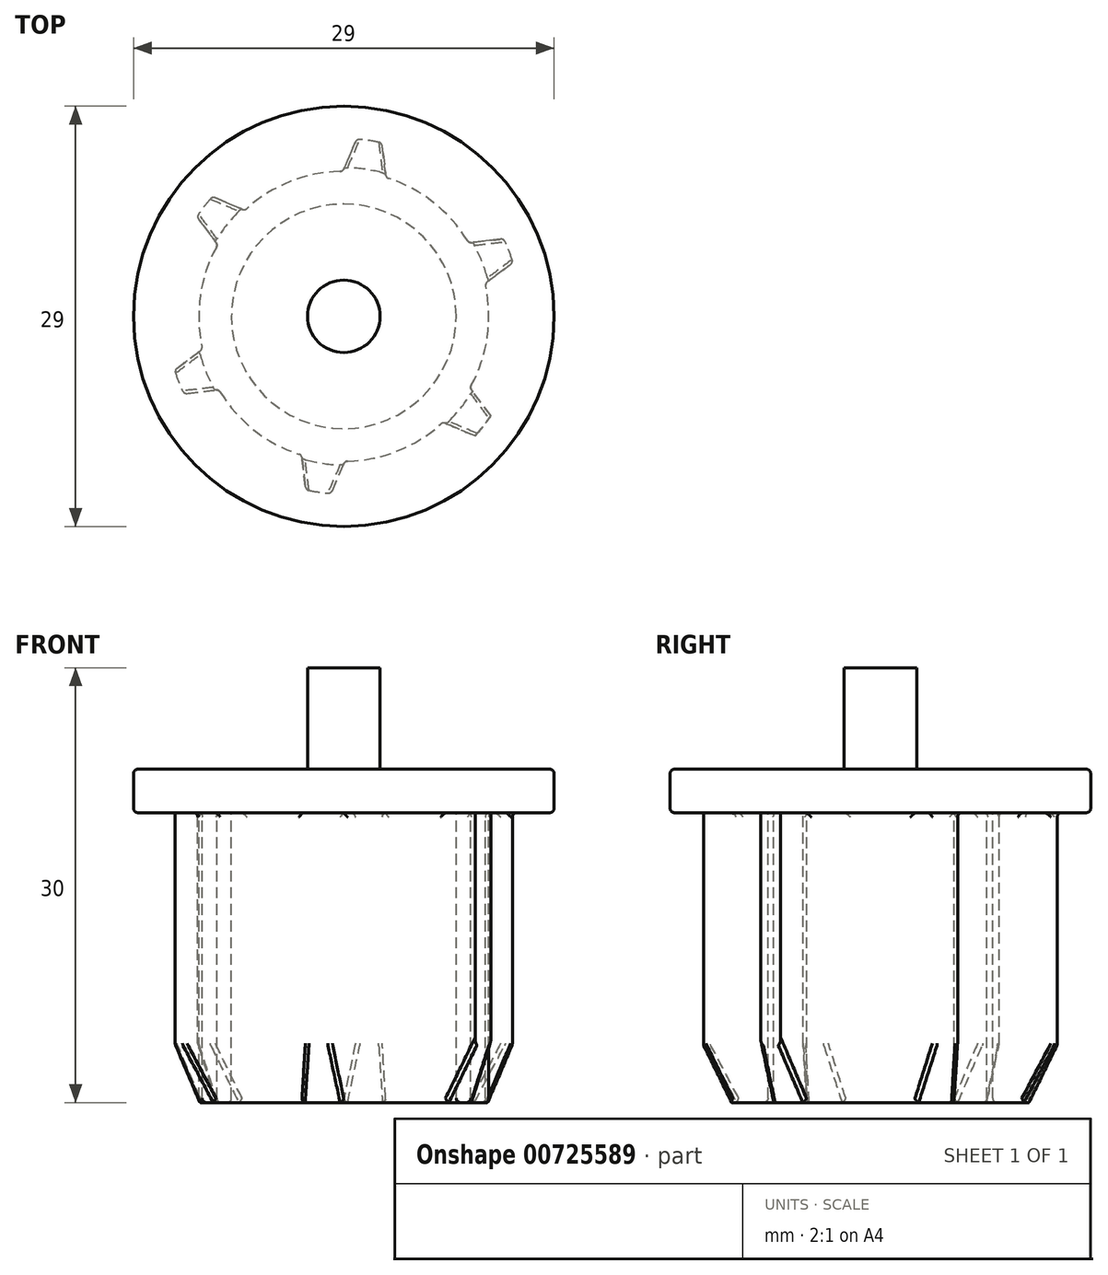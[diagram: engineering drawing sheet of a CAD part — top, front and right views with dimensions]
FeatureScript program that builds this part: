
annotation { "Feature Type Name" : "Feature", "Feature Type Description" : "" }
export const myFeature = defineFeature(function(context is Context, id is Id, definition is map)
    precondition{}
    {
        {
            var Q0;
            Q0=qCreatedBy(makeId("Top.planeOp"),FACE);
            var sketch = newSketch(context, id + "F0", { "sketchPlane" : qUnion([Q0])});
            skCircle(sketch, "E0", {"center": v(-16.6, 0) * mm, "radius": 14.5 * mm});
            skCircle(sketch, "E1", {"center": v(-16.6, 0) * mm, "radius": 12.25 * mm});
            skCircle(sketch, "E2", {"center": v(-16.6, 0) * mm, "radius": 4 * mm, "construction": true});
            skCircle(sketch, "E3.cCircle", {"center": v(-16.6, 0) * mm, "radius": 15 * mm, "construction": true});
            skLineSegment(sketch, "E3.0", {"start": v(-6.99, 12.2) * mm, "end": v(-2.18, 5.76) * mm});
            skLineSegment(sketch, "E3.1", {"start": v(-2.18, 5.76) * mm, "end": v(-1.23, -2.23) * mm});
            skLineSegment(sketch, "E3.2", {"start": v(-1.23, -2.23) * mm, "end": v(-4.4, -9.61) * mm});
            skLineSegment(sketch, "E3.3", {"start": v(-4.4, -9.61) * mm, "end": v(-10.84, -14.42) * mm});
            skLineSegment(sketch, "E3.4", {"start": v(-10.84, -14.42) * mm, "end": v(-18.83, -15.37) * mm});
            skLineSegment(sketch, "E3.5", {"start": v(-18.83, -15.37) * mm, "end": v(-26.21, -12.2) * mm});
            skLineSegment(sketch, "E3.6", {"start": v(-26.21, -12.2) * mm, "end": v(-31.02, -5.76) * mm});
            skLineSegment(sketch, "E3.7", {"start": v(-31.02, -5.76) * mm, "end": v(-31.97, 2.23) * mm});
            skLineSegment(sketch, "E3.8", {"start": v(-31.97, 2.23) * mm, "end": v(-28.8, 9.61) * mm});
            skLineSegment(sketch, "E3.9", {"start": v(-28.8, 9.61) * mm, "end": v(-22.36, 14.42) * mm});
            skLineSegment(sketch, "E3.10", {"start": v(-22.36, 14.42) * mm, "end": v(-14.37, 15.37) * mm});
            skLineSegment(sketch, "E3.11", {"start": v(-14.37, 15.37) * mm, "end": v(-6.99, 12.2) * mm});
            skPoint(sketch, "E3.0.midPoint", {"position": v(-4.58, 8.98) * mm});
            skLineSegment(sketch, "E4", {"start": v(-18.83, -15.37) * mm, "end": v(-20.57, -0.47) * mm});
            skLineSegment(sketch, "E5", {"start": v(-18.83, -15.37) * mm, "end": v(-12.92, -1.57) * mm});
            skLineSegment(sketch, "E6", {"start": v(-4.4, -9.61) * mm, "end": v(-18.18, -3.67) * mm});
            skLineSegment(sketch, "E7", {"start": v(-4.4, -9.61) * mm, "end": v(-13.4, 2.4) * mm});
            skLineSegment(sketch, "E8", {"start": v(-2.18, 5.76) * mm, "end": v(-14.21, -3.2) * mm});
            skLineSegment(sketch, "E9", {"start": v(-2.18, 5.76) * mm, "end": v(-17.08, 3.97) * mm});
            skLineSegment(sketch, "E10", {"start": v(-14.37, 15.37) * mm, "end": v(-12.63, 0.47) * mm});
            skLineSegment(sketch, "E11", {"start": v(-14.37, 15.37) * mm, "end": v(-20.28, 1.57) * mm});
            skLineSegment(sketch, "E12", {"start": v(-28.8, 9.61) * mm, "end": v(-15.02, 3.67) * mm});
            skLineSegment(sketch, "E13", {"start": v(-28.8, 9.61) * mm, "end": v(-19.8, -2.4) * mm});
            skLineSegment(sketch, "E14", {"start": v(-31.02, -5.76) * mm, "end": v(-18.99, 3.2) * mm});
            skLineSegment(sketch, "E15", {"start": v(-31.02, -5.76) * mm, "end": v(-16.12, -3.97) * mm});
            skCircle(sketch, "E16", {"center": v(-16.6, 0) * mm, "radius": 10 * mm});
            skCircle(sketch, "E17", {"center": v(-16.6, 0) * mm, "radius": 7.75 * mm});
            skCircle(sketch, "E18", {"center": v(-16.6, 0) * mm, "radius": 2.5 * mm});
            skSolve(sketch);
        }
        {
            var Q0;
            Q0=qCreatedBy(makeId("Front.planeOp"),FACE);
            var sketch = newSketch(context, id + "F1", { "sketchPlane" : qUnion([Q0])});
            skLineSegment(sketch, "E19", {"start": v(-32.68, -23) * mm, "end": v(-0.52, -23) * mm});
            skLineSegment(sketch, "E20", {"start": v(-32.68, -20) * mm, "end": v(-0.52, -20) * mm});
            skLineSegment(sketch, "E21", {"start": v(-32.68, -3) * mm, "end": v(-0.52, -3) * mm});
            skLineSegment(sketch, "E22", {"start": v(-32.68, 0) * mm, "end": v(-0.52, 0) * mm});
            skSolve(sketch);
        }
        {
            var Q0;
            {var subQ0=sQuery(id+"F0.wireOp",EDGE,"E16");var subQ1=sQuery(id+"F0.wireOp",EDGE,"E9");var subQ2=makeQuery(id+"F0.imprint","INTERSECT",VERTEX,{"derivedFrom":[subQ1,subQ0]});Q0=makeQuery(id+"F0.imprint","IMPRINT",FACE,{"disambiguationData":[TD([[makeQuery(id+"F0.imprint","IMPRINT",EDGE,{"disambiguationData":[TD([[subQ2,-1.0]])],"derivedFrom":subQ1}),-1.0]])]});}
            var Q1;
            {var subQ0=sQuery(id+"F0.wireOp",EDGE,"E9");var subQ1=sQuery(id+"F0.wireOp",EDGE,"E1");var subQ2=makeQuery(id+"F0.imprint","INTERSECT",VERTEX,{"derivedFrom":[subQ1,subQ0]});Q1=makeQuery(id+"F0.imprint","IMPRINT",FACE,{"disambiguationData":[TD([[makeQuery(id+"F0.imprint","IMPRINT",EDGE,{"disambiguationData":[TD([[subQ2,1.0]])],"derivedFrom":subQ1}),1.0]])]});}
            var Q2;
            {var subQ0=sQuery(id+"F0.wireOp",EDGE,"E16");var subQ1=sQuery(id+"F0.wireOp",EDGE,"E8");var subQ2=makeQuery(id+"F0.imprint","INTERSECT",VERTEX,{"derivedFrom":[subQ1,subQ0]});Q2=makeQuery(id+"F0.imprint","IMPRINT",FACE,{"disambiguationData":[TD([[makeQuery(id+"F0.imprint","IMPRINT",EDGE,{"disambiguationData":[TD([[subQ2,-1.0]])],"derivedFrom":subQ1}),-1.0]])]});}
            var Q3;
            {var subQ0=sQuery(id+"F0.wireOp",EDGE,"E16");var subQ1=sQuery(id+"F0.wireOp",EDGE,"E7");var subQ2=makeQuery(id+"F0.imprint","INTERSECT",VERTEX,{"derivedFrom":[subQ1,subQ0]});Q3=makeQuery(id+"F0.imprint","IMPRINT",FACE,{"disambiguationData":[TD([[makeQuery(id+"F0.imprint","IMPRINT",EDGE,{"disambiguationData":[TD([[subQ2,-1.0]])],"derivedFrom":subQ1}),-1.0]])]});}
            var Q4;
            {var subQ0=sQuery(id+"F0.wireOp",EDGE,"E6");var subQ1=sQuery(id+"F0.wireOp",EDGE,"E1");var subQ2=makeQuery(id+"F0.imprint","INTERSECT",VERTEX,{"derivedFrom":[subQ1,subQ0]});Q4=makeQuery(id+"F0.imprint","IMPRINT",FACE,{"disambiguationData":[TD([[makeQuery(id+"F0.imprint","IMPRINT",EDGE,{"disambiguationData":[TD([[subQ2,-1.0]])],"derivedFrom":subQ1}),1.0]])]});}
            var Q5;
            {var subQ0=sQuery(id+"F0.wireOp",EDGE,"E16");var subQ1=sQuery(id+"F0.wireOp",EDGE,"E6");var subQ2=makeQuery(id+"F0.imprint","INTERSECT",VERTEX,{"derivedFrom":[subQ1,subQ0]});Q5=makeQuery(id+"F0.imprint","IMPRINT",FACE,{"disambiguationData":[TD([[makeQuery(id+"F0.imprint","IMPRINT",EDGE,{"disambiguationData":[TD([[subQ2,-1.0]])],"derivedFrom":subQ1}),-1.0]])]});}
            var Q6;
            {var subQ0=sQuery(id+"F0.wireOp",EDGE,"E16");var subQ1=sQuery(id+"F0.wireOp",EDGE,"E5");var subQ2=makeQuery(id+"F0.imprint","INTERSECT",VERTEX,{"derivedFrom":[subQ1,subQ0]});Q6=makeQuery(id+"F0.imprint","IMPRINT",FACE,{"disambiguationData":[TD([[makeQuery(id+"F0.imprint","IMPRINT",EDGE,{"disambiguationData":[TD([[subQ2,-1.0]])],"derivedFrom":subQ1}),-1.0]])]});}
            var Q7;
            {var subQ0=sQuery(id+"F0.wireOp",EDGE,"E16");var subQ1=sQuery(id+"F0.wireOp",EDGE,"E4");var subQ2=makeQuery(id+"F0.imprint","INTERSECT",VERTEX,{"derivedFrom":[subQ1,subQ0]});Q7=makeQuery(id+"F0.imprint","IMPRINT",FACE,{"disambiguationData":[TD([[makeQuery(id+"F0.imprint","IMPRINT",EDGE,{"disambiguationData":[TD([[subQ2,-1.0]])],"derivedFrom":subQ1}),-1.0]])]});}
            var Q8;
            {var subQ0=sQuery(id+"F0.wireOp",EDGE,"E4");var subQ1=sQuery(id+"F0.wireOp",EDGE,"E1");var subQ2=makeQuery(id+"F0.imprint","INTERSECT",VERTEX,{"derivedFrom":[subQ1,subQ0]});Q8=makeQuery(id+"F0.imprint","IMPRINT",FACE,{"disambiguationData":[TD([[makeQuery(id+"F0.imprint","IMPRINT",EDGE,{"disambiguationData":[TD([[subQ2,-1.0]])],"derivedFrom":subQ1}),1.0]])]});}
            var Q9;
            {var subQ0=sQuery(id+"F0.wireOp",EDGE,"E16");var subQ1=sQuery(id+"F0.wireOp",EDGE,"E4");var subQ2=makeQuery(id+"F0.imprint","INTERSECT",VERTEX,{"derivedFrom":[subQ1,subQ0]});Q9=makeQuery(id+"F0.imprint","IMPRINT",FACE,{"disambiguationData":[TD([[makeQuery(id+"F0.imprint","IMPRINT",EDGE,{"disambiguationData":[TD([[subQ2,-1.0]])],"derivedFrom":subQ1}),1.0]])]});}
            var Q10;
            {var subQ0=sQuery(id+"F0.wireOp",EDGE,"E16");var subQ1=sQuery(id+"F0.wireOp",EDGE,"E14");var subQ2=makeQuery(id+"F0.imprint","INTERSECT",VERTEX,{"derivedFrom":[subQ1,subQ0]});Q10=makeQuery(id+"F0.imprint","IMPRINT",FACE,{"disambiguationData":[TD([[makeQuery(id+"F0.imprint","IMPRINT",EDGE,{"disambiguationData":[TD([[subQ2,-1.0]])],"derivedFrom":subQ1}),-1.0]])]});}
            var Q11;
            {var subQ0=sQuery(id+"F0.wireOp",EDGE,"E14");var subQ1=sQuery(id+"F0.wireOp",EDGE,"E1");var subQ2=makeQuery(id+"F0.imprint","INTERSECT",VERTEX,{"derivedFrom":[subQ1,subQ0]});Q11=makeQuery(id+"F0.imprint","IMPRINT",FACE,{"disambiguationData":[TD([[makeQuery(id+"F0.imprint","IMPRINT",EDGE,{"disambiguationData":[TD([[subQ2,-1.0]])],"derivedFrom":subQ1}),1.0]])]});}
            var Q12;
            {var subQ0=sQuery(id+"F0.wireOp",EDGE,"E16");var subQ1=sQuery(id+"F0.wireOp",EDGE,"E13");var subQ2=makeQuery(id+"F0.imprint","INTERSECT",VERTEX,{"derivedFrom":[subQ1,subQ0]});Q12=makeQuery(id+"F0.imprint","IMPRINT",FACE,{"disambiguationData":[TD([[makeQuery(id+"F0.imprint","IMPRINT",EDGE,{"disambiguationData":[TD([[subQ2,-1.0]])],"derivedFrom":subQ1}),-1.0]])]});}
            var Q13;
            {var subQ0=sQuery(id+"F0.wireOp",EDGE,"E16");var subQ1=sQuery(id+"F0.wireOp",EDGE,"E12");var subQ2=makeQuery(id+"F0.imprint","INTERSECT",VERTEX,{"derivedFrom":[subQ1,subQ0]});Q13=makeQuery(id+"F0.imprint","IMPRINT",FACE,{"disambiguationData":[TD([[makeQuery(id+"F0.imprint","IMPRINT",EDGE,{"disambiguationData":[TD([[subQ2,-1.0]])],"derivedFrom":subQ1}),-1.0]])]});}
            var Q14;
            {var subQ0=sQuery(id+"F0.wireOp",EDGE,"E12");var subQ1=sQuery(id+"F0.wireOp",EDGE,"E1");var subQ2=makeQuery(id+"F0.imprint","INTERSECT",VERTEX,{"derivedFrom":[subQ1,subQ0]});Q14=makeQuery(id+"F0.imprint","IMPRINT",FACE,{"disambiguationData":[TD([[makeQuery(id+"F0.imprint","IMPRINT",EDGE,{"disambiguationData":[TD([[subQ2,-1.0]])],"derivedFrom":subQ1}),1.0]])]});}
            var Q15;
            {var subQ0=sQuery(id+"F0.wireOp",EDGE,"E16");var subQ1=sQuery(id+"F0.wireOp",EDGE,"E11");var subQ2=makeQuery(id+"F0.imprint","INTERSECT",VERTEX,{"derivedFrom":[subQ1,subQ0]});Q15=makeQuery(id+"F0.imprint","IMPRINT",FACE,{"disambiguationData":[TD([[makeQuery(id+"F0.imprint","IMPRINT",EDGE,{"disambiguationData":[TD([[subQ2,-1.0]])],"derivedFrom":subQ1}),-1.0]])]});}
            var Q16;
            {var subQ0=sQuery(id+"F0.wireOp",EDGE,"E16");var subQ1=sQuery(id+"F0.wireOp",EDGE,"E10");var subQ2=makeQuery(id+"F0.imprint","INTERSECT",VERTEX,{"derivedFrom":[subQ1,subQ0]});Q16=makeQuery(id+"F0.imprint","IMPRINT",FACE,{"disambiguationData":[TD([[makeQuery(id+"F0.imprint","IMPRINT",EDGE,{"disambiguationData":[TD([[subQ2,-1.0]])],"derivedFrom":subQ1}),-1.0]])]});}
            var Q17;
            {var subQ0=sQuery(id+"F0.wireOp",EDGE,"E10");var subQ1=sQuery(id+"F0.wireOp",EDGE,"E1");var subQ2=makeQuery(id+"F0.imprint","INTERSECT",VERTEX,{"derivedFrom":[subQ1,subQ0]});Q17=makeQuery(id+"F0.imprint","IMPRINT",FACE,{"disambiguationData":[TD([[makeQuery(id+"F0.imprint","IMPRINT",EDGE,{"disambiguationData":[TD([[subQ2,-1.0]])],"derivedFrom":subQ1}),1.0]])]});}
            var Q18;
            Q18=sQuery(id+"F1.wireOp",VERTEX,"E19.start");
            extrude(context, id + "F2", {"entities" : qUnion([Q0, Q1, Q2, Q3, Q4, Q5, Q6, Q7, Q8, Q9, Q10, Q11, Q12, Q13, Q14, Q15, Q16, Q17]), "endBound" : BoundingType.UP_TO_VERTEX, "oppositeDirection" : true, "depth" : 25 * mm, "endBoundEntityVertex" : qUnion([Q18]), "offsetDistance" : 25 * mm});
        }
        {
            var Q0;
            {var subQ0=sQuery(id+"F0.wireOp",EDGE,"E11");var subQ1=sQuery(id+"F0.wireOp",EDGE,"E1");var subQ2=makeQuery(id+"F0.imprint","INTERSECT",VERTEX,{"derivedFrom":[subQ1,subQ0]});Q0=makeQuery(id+"F0.imprint","IMPRINT",FACE,{"disambiguationData":[TD([[makeQuery(id+"F0.imprint","IMPRINT",EDGE,{"disambiguationData":[TD([[subQ2,-1.0]])],"derivedFrom":subQ1}),1.0]])]});}
            var Q1;
            {var subQ0=sQuery(id+"F0.wireOp",EDGE,"E11");var subQ1=sQuery(id+"F0.wireOp",EDGE,"E0");var subQ2=makeQuery(id+"F0.imprint","INTERSECT",VERTEX,{"derivedFrom":[subQ1,subQ0]});Q1=makeQuery(id+"F0.imprint","IMPRINT",FACE,{"disambiguationData":[TD([[makeQuery(id+"F0.imprint","IMPRINT",EDGE,{"disambiguationData":[TD([[subQ2,-1.0]])],"derivedFrom":subQ1}),1.0]])]});}
            var Q2;
            {var subQ0=sQuery(id+"F0.wireOp",EDGE,"E10");var subQ1=sQuery(id+"F0.wireOp",EDGE,"E0");var subQ2=makeQuery(id+"F0.imprint","INTERSECT",VERTEX,{"derivedFrom":[subQ1,subQ0]});Q2=makeQuery(id+"F0.imprint","IMPRINT",FACE,{"disambiguationData":[TD([[makeQuery(id+"F0.imprint","IMPRINT",EDGE,{"disambiguationData":[TD([[subQ2,-1.0]])],"derivedFrom":subQ1}),1.0]])]});}
            var Q3;
            {var subQ0=sQuery(id+"F0.wireOp",EDGE,"E9");var subQ1=sQuery(id+"F0.wireOp",EDGE,"E0");var subQ2=makeQuery(id+"F0.imprint","INTERSECT",VERTEX,{"derivedFrom":[subQ1,subQ0]});Q3=makeQuery(id+"F0.imprint","IMPRINT",FACE,{"disambiguationData":[TD([[makeQuery(id+"F0.imprint","IMPRINT",EDGE,{"disambiguationData":[TD([[subQ2,-1.0]])],"derivedFrom":subQ1}),1.0]])]});}
            var Q4;
            {var subQ0=sQuery(id+"F0.wireOp",EDGE,"E9");var subQ1=sQuery(id+"F0.wireOp",EDGE,"E1");var subQ2=makeQuery(id+"F0.imprint","INTERSECT",VERTEX,{"derivedFrom":[subQ1,subQ0]});Q4=makeQuery(id+"F0.imprint","IMPRINT",FACE,{"disambiguationData":[TD([[makeQuery(id+"F0.imprint","IMPRINT",EDGE,{"disambiguationData":[TD([[subQ2,-1.0]])],"derivedFrom":subQ1}),1.0]])]});}
            var Q5;
            {var subQ0=sQuery(id+"F0.wireOp",EDGE,"E10");var subQ1=sQuery(id+"F0.wireOp",EDGE,"E1");var subQ2=makeQuery(id+"F0.imprint","INTERSECT",VERTEX,{"derivedFrom":[subQ1,subQ0]});Q5=makeQuery(id+"F0.imprint","IMPRINT",FACE,{"disambiguationData":[TD([[makeQuery(id+"F0.imprint","IMPRINT",EDGE,{"disambiguationData":[TD([[subQ2,-1.0]])],"derivedFrom":subQ1}),1.0]])]});}
            var Q6;
            {var subQ0=sQuery(id+"F0.wireOp",EDGE,"E16");var subQ1=sQuery(id+"F0.wireOp",EDGE,"E9");var subQ2=makeQuery(id+"F0.imprint","INTERSECT",VERTEX,{"derivedFrom":[subQ1,subQ0]});Q6=makeQuery(id+"F0.imprint","IMPRINT",FACE,{"disambiguationData":[TD([[makeQuery(id+"F0.imprint","IMPRINT",EDGE,{"disambiguationData":[TD([[subQ2,-1.0]])],"derivedFrom":subQ1}),-1.0]])]});}
            var Q7;
            {var subQ0=sQuery(id+"F0.wireOp",EDGE,"E16");var subQ1=sQuery(id+"F0.wireOp",EDGE,"E8");var subQ2=makeQuery(id+"F0.imprint","INTERSECT",VERTEX,{"derivedFrom":[subQ1,subQ0]});Q7=makeQuery(id+"F0.imprint","IMPRINT",FACE,{"disambiguationData":[TD([[makeQuery(id+"F0.imprint","IMPRINT",EDGE,{"disambiguationData":[TD([[subQ2,-1.0]])],"derivedFrom":subQ1}),-1.0]])]});}
            var Q8;
            {var subQ0=sQuery(id+"F0.wireOp",EDGE,"E9");var subQ1=sQuery(id+"F0.wireOp",EDGE,"E1");var subQ2=makeQuery(id+"F0.imprint","INTERSECT",VERTEX,{"derivedFrom":[subQ1,subQ0]});Q8=makeQuery(id+"F0.imprint","IMPRINT",FACE,{"disambiguationData":[TD([[makeQuery(id+"F0.imprint","IMPRINT",EDGE,{"disambiguationData":[TD([[subQ2,1.0]])],"derivedFrom":subQ1}),1.0]])]});}
            var Q9;
            {var subQ0=sQuery(id+"F0.wireOp",EDGE,"E9");var subQ1=sQuery(id+"F0.wireOp",EDGE,"E0");var subQ2=makeQuery(id+"F0.imprint","INTERSECT",VERTEX,{"derivedFrom":[subQ1,subQ0]});Q9=makeQuery(id+"F0.imprint","IMPRINT",FACE,{"disambiguationData":[TD([[makeQuery(id+"F0.imprint","IMPRINT",EDGE,{"disambiguationData":[TD([[subQ2,1.0]])],"derivedFrom":subQ1}),1.0]])]});}
            var Q10;
            {var subQ0=sQuery(id+"F0.wireOp",EDGE,"E8");var subQ1=sQuery(id+"F0.wireOp",EDGE,"E1");var subQ2=makeQuery(id+"F0.imprint","INTERSECT",VERTEX,{"derivedFrom":[subQ1,subQ0]});Q10=makeQuery(id+"F0.imprint","IMPRINT",FACE,{"disambiguationData":[TD([[makeQuery(id+"F0.imprint","IMPRINT",EDGE,{"disambiguationData":[TD([[subQ2,1.0]])],"derivedFrom":subQ1}),1.0]])]});}
            var Q11;
            {var subQ0=sQuery(id+"F0.wireOp",EDGE,"E5");var subQ1=sQuery(id+"F0.wireOp",EDGE,"E0");var subQ2=makeQuery(id+"F0.imprint","INTERSECT",VERTEX,{"derivedFrom":[subQ1,subQ0]});Q11=makeQuery(id+"F0.imprint","IMPRINT",FACE,{"disambiguationData":[TD([[makeQuery(id+"F0.imprint","IMPRINT",EDGE,{"disambiguationData":[TD([[subQ2,-1.0]])],"derivedFrom":subQ1}),1.0]])]});}
            var Q12;
            {var subQ0=sQuery(id+"F0.wireOp",EDGE,"E4");var subQ1=sQuery(id+"F0.wireOp",EDGE,"E0");var subQ2=makeQuery(id+"F0.imprint","INTERSECT",VERTEX,{"derivedFrom":[subQ1,subQ0]});Q12=makeQuery(id+"F0.imprint","IMPRINT",FACE,{"disambiguationData":[TD([[makeQuery(id+"F0.imprint","IMPRINT",EDGE,{"disambiguationData":[TD([[subQ2,-1.0]])],"derivedFrom":subQ1}),1.0]])]});}
            var Q13;
            {var subQ0=sQuery(id+"F0.wireOp",EDGE,"E4");var subQ1=sQuery(id+"F0.wireOp",EDGE,"E1");var subQ2=makeQuery(id+"F0.imprint","INTERSECT",VERTEX,{"derivedFrom":[subQ1,subQ0]});Q13=makeQuery(id+"F0.imprint","IMPRINT",FACE,{"disambiguationData":[TD([[makeQuery(id+"F0.imprint","IMPRINT",EDGE,{"disambiguationData":[TD([[subQ2,-1.0]])],"derivedFrom":subQ1}),1.0]])]});}
            var Q14;
            {var subQ0=sQuery(id+"F0.wireOp",EDGE,"E14");var subQ1=sQuery(id+"F0.wireOp",EDGE,"E1");var subQ2=makeQuery(id+"F0.imprint","INTERSECT",VERTEX,{"derivedFrom":[subQ1,subQ0]});Q14=makeQuery(id+"F0.imprint","IMPRINT",FACE,{"disambiguationData":[TD([[makeQuery(id+"F0.imprint","IMPRINT",EDGE,{"disambiguationData":[TD([[subQ2,-1.0]])],"derivedFrom":subQ1}),1.0]])]});}
            var Q15;
            {var subQ0=sQuery(id+"F0.wireOp",EDGE,"E16");var subQ1=sQuery(id+"F0.wireOp",EDGE,"E14");var subQ2=makeQuery(id+"F0.imprint","INTERSECT",VERTEX,{"derivedFrom":[subQ1,subQ0]});Q15=makeQuery(id+"F0.imprint","IMPRINT",FACE,{"disambiguationData":[TD([[makeQuery(id+"F0.imprint","IMPRINT",EDGE,{"disambiguationData":[TD([[subQ2,-1.0]])],"derivedFrom":subQ1}),-1.0]])]});}
            var Q16;
            {var subQ0=sQuery(id+"F0.wireOp",EDGE,"E8");var subQ1=sQuery(id+"F0.wireOp",EDGE,"E0");var subQ2=makeQuery(id+"F0.imprint","INTERSECT",VERTEX,{"derivedFrom":[subQ1,subQ0]});Q16=makeQuery(id+"F0.imprint","IMPRINT",FACE,{"disambiguationData":[TD([[makeQuery(id+"F0.imprint","IMPRINT",EDGE,{"disambiguationData":[TD([[subQ2,1.0]])],"derivedFrom":subQ1}),1.0]])]});}
            var Q17;
            {var subQ0=sQuery(id+"F0.wireOp",EDGE,"E6");var subQ1=sQuery(id+"F0.wireOp",EDGE,"E0");var subQ2=makeQuery(id+"F0.imprint","INTERSECT",VERTEX,{"derivedFrom":[subQ1,subQ0]});Q17=makeQuery(id+"F0.imprint","IMPRINT",FACE,{"disambiguationData":[TD([[makeQuery(id+"F0.imprint","IMPRINT",EDGE,{"disambiguationData":[TD([[subQ2,-1.0]])],"derivedFrom":subQ1}),1.0]])]});}
            var Q18;
            {var subQ0=sQuery(id+"F0.wireOp",EDGE,"E6");var subQ1=sQuery(id+"F0.wireOp",EDGE,"E1");var subQ2=makeQuery(id+"F0.imprint","INTERSECT",VERTEX,{"derivedFrom":[subQ1,subQ0]});Q18=makeQuery(id+"F0.imprint","IMPRINT",FACE,{"disambiguationData":[TD([[makeQuery(id+"F0.imprint","IMPRINT",EDGE,{"disambiguationData":[TD([[subQ2,-1.0]])],"derivedFrom":subQ1}),1.0]])]});}
            var Q19;
            {var subQ0=sQuery(id+"F0.wireOp",EDGE,"E5");var subQ1=sQuery(id+"F0.wireOp",EDGE,"E1");var subQ2=makeQuery(id+"F0.imprint","INTERSECT",VERTEX,{"derivedFrom":[subQ1,subQ0]});Q19=makeQuery(id+"F0.imprint","IMPRINT",FACE,{"disambiguationData":[TD([[makeQuery(id+"F0.imprint","IMPRINT",EDGE,{"disambiguationData":[TD([[subQ2,-1.0]])],"derivedFrom":subQ1}),1.0]])]});}
            var Q20;
            {var subQ0=sQuery(id+"F0.wireOp",EDGE,"E15");var subQ1=sQuery(id+"F0.wireOp",EDGE,"E1");var subQ2=makeQuery(id+"F0.imprint","INTERSECT",VERTEX,{"derivedFrom":[subQ1,subQ0]});Q20=makeQuery(id+"F0.imprint","IMPRINT",FACE,{"disambiguationData":[TD([[makeQuery(id+"F0.imprint","IMPRINT",EDGE,{"disambiguationData":[TD([[subQ2,-1.0]])],"derivedFrom":subQ1}),1.0]])]});}
            var Q21;
            {var subQ0=sQuery(id+"F0.wireOp",EDGE,"E15");var subQ1=sQuery(id+"F0.wireOp",EDGE,"E0");var subQ2=makeQuery(id+"F0.imprint","INTERSECT",VERTEX,{"derivedFrom":[subQ1,subQ0]});Q21=makeQuery(id+"F0.imprint","IMPRINT",FACE,{"disambiguationData":[TD([[makeQuery(id+"F0.imprint","IMPRINT",EDGE,{"disambiguationData":[TD([[subQ2,-1.0]])],"derivedFrom":subQ1}),1.0]])]});}
            var Q22;
            {var subQ0=sQuery(id+"F0.wireOp",EDGE,"E14");var subQ1=sQuery(id+"F0.wireOp",EDGE,"E0");var subQ2=makeQuery(id+"F0.imprint","INTERSECT",VERTEX,{"derivedFrom":[subQ1,subQ0]});Q22=makeQuery(id+"F0.imprint","IMPRINT",FACE,{"disambiguationData":[TD([[makeQuery(id+"F0.imprint","IMPRINT",EDGE,{"disambiguationData":[TD([[subQ2,-1.0]])],"derivedFrom":subQ1}),1.0]])]});}
            var Q23;
            {var subQ0=sQuery(id+"F0.wireOp",EDGE,"E13");var subQ1=sQuery(id+"F0.wireOp",EDGE,"E0");var subQ2=makeQuery(id+"F0.imprint","INTERSECT",VERTEX,{"derivedFrom":[subQ1,subQ0]});Q23=makeQuery(id+"F0.imprint","IMPRINT",FACE,{"disambiguationData":[TD([[makeQuery(id+"F0.imprint","IMPRINT",EDGE,{"disambiguationData":[TD([[subQ2,-1.0]])],"derivedFrom":subQ1}),1.0]])]});}
            var Q24;
            {var subQ0=sQuery(id+"F0.wireOp",EDGE,"E13");var subQ1=sQuery(id+"F0.wireOp",EDGE,"E1");var subQ2=makeQuery(id+"F0.imprint","INTERSECT",VERTEX,{"derivedFrom":[subQ1,subQ0]});Q24=makeQuery(id+"F0.imprint","IMPRINT",FACE,{"disambiguationData":[TD([[makeQuery(id+"F0.imprint","IMPRINT",EDGE,{"disambiguationData":[TD([[subQ2,-1.0]])],"derivedFrom":subQ1}),1.0]])]});}
            var Q25;
            {var subQ0=sQuery(id+"F0.wireOp",EDGE,"E16");var subQ1=sQuery(id+"F0.wireOp",EDGE,"E13");var subQ2=makeQuery(id+"F0.imprint","INTERSECT",VERTEX,{"derivedFrom":[subQ1,subQ0]});Q25=makeQuery(id+"F0.imprint","IMPRINT",FACE,{"disambiguationData":[TD([[makeQuery(id+"F0.imprint","IMPRINT",EDGE,{"disambiguationData":[TD([[subQ2,-1.0]])],"derivedFrom":subQ1}),-1.0]])]});}
            var Q26;
            {var subQ0=sQuery(id+"F0.wireOp",EDGE,"E12");var subQ1=sQuery(id+"F0.wireOp",EDGE,"E0");var subQ2=makeQuery(id+"F0.imprint","INTERSECT",VERTEX,{"derivedFrom":[subQ1,subQ0]});Q26=makeQuery(id+"F0.imprint","IMPRINT",FACE,{"disambiguationData":[TD([[makeQuery(id+"F0.imprint","IMPRINT",EDGE,{"disambiguationData":[TD([[subQ2,-1.0]])],"derivedFrom":subQ1}),1.0]])]});}
            var Q27;
            {var subQ0=sQuery(id+"F0.wireOp",EDGE,"E12");var subQ1=sQuery(id+"F0.wireOp",EDGE,"E1");var subQ2=makeQuery(id+"F0.imprint","INTERSECT",VERTEX,{"derivedFrom":[subQ1,subQ0]});Q27=makeQuery(id+"F0.imprint","IMPRINT",FACE,{"disambiguationData":[TD([[makeQuery(id+"F0.imprint","IMPRINT",EDGE,{"disambiguationData":[TD([[subQ2,-1.0]])],"derivedFrom":subQ1}),1.0]])]});}
            var Q28;
            {var subQ0=sQuery(id+"F0.wireOp",EDGE,"E16");var subQ1=sQuery(id+"F0.wireOp",EDGE,"E12");var subQ2=makeQuery(id+"F0.imprint","INTERSECT",VERTEX,{"derivedFrom":[subQ1,subQ0]});Q28=makeQuery(id+"F0.imprint","IMPRINT",FACE,{"disambiguationData":[TD([[makeQuery(id+"F0.imprint","IMPRINT",EDGE,{"disambiguationData":[TD([[subQ2,-1.0]])],"derivedFrom":subQ1}),-1.0]])]});}
            var Q29;
            {var subQ0=sQuery(id+"F0.wireOp",EDGE,"E16");var subQ1=sQuery(id+"F0.wireOp",EDGE,"E11");var subQ2=makeQuery(id+"F0.imprint","INTERSECT",VERTEX,{"derivedFrom":[subQ1,subQ0]});Q29=makeQuery(id+"F0.imprint","IMPRINT",FACE,{"disambiguationData":[TD([[makeQuery(id+"F0.imprint","IMPRINT",EDGE,{"disambiguationData":[TD([[subQ2,-1.0]])],"derivedFrom":subQ1}),-1.0]])]});}
            var Q30;
            {var subQ0=sQuery(id+"F0.wireOp",EDGE,"E16");var subQ1=sQuery(id+"F0.wireOp",EDGE,"E10");var subQ2=makeQuery(id+"F0.imprint","INTERSECT",VERTEX,{"derivedFrom":[subQ1,subQ0]});Q30=makeQuery(id+"F0.imprint","IMPRINT",FACE,{"disambiguationData":[TD([[makeQuery(id+"F0.imprint","IMPRINT",EDGE,{"disambiguationData":[TD([[subQ2,-1.0]])],"derivedFrom":subQ1}),-1.0]])]});}
            var Q31;
            {var subQ0=sQuery(id+"F0.wireOp",EDGE,"E12");var subQ1=sQuery(id+"F0.wireOp",EDGE,"E9");var subQ2=makeQuery(id+"F0.imprint","INTERSECT",VERTEX,{"derivedFrom":[subQ1,subQ0]});Q31=makeQuery(id+"F0.imprint","IMPRINT",FACE,{"disambiguationData":[TD([[makeQuery(id+"F0.imprint","IMPRINT",EDGE,{"disambiguationData":[TD([[subQ2,1.0]])],"derivedFrom":subQ1}),-1.0]])]});}
            var Q32;
            {var subQ0=sQuery(id+"F0.wireOp",EDGE,"E17");var subQ1=sQuery(id+"F0.wireOp",EDGE,"E9");var subQ2=makeQuery(id+"F0.imprint","INTERSECT",VERTEX,{"derivedFrom":[subQ1,subQ0]});Q32=makeQuery(id+"F0.imprint","IMPRINT",FACE,{"disambiguationData":[TD([[makeQuery(id+"F0.imprint","IMPRINT",EDGE,{"disambiguationData":[TD([[subQ2,-1.0]])],"derivedFrom":subQ1}),-1.0]])]});}
            var Q33;
            {var subQ0=sQuery(id+"F0.wireOp",EDGE,"E10");var subQ1=sQuery(id+"F0.wireOp",EDGE,"E7");var subQ2=makeQuery(id+"F0.imprint","INTERSECT",VERTEX,{"derivedFrom":[subQ1,subQ0]});Q33=makeQuery(id+"F0.imprint","IMPRINT",FACE,{"disambiguationData":[TD([[makeQuery(id+"F0.imprint","IMPRINT",EDGE,{"disambiguationData":[TD([[subQ2,1.0]])],"derivedFrom":subQ1}),-1.0]])]});}
            var Q34;
            {var subQ0=sQuery(id+"F0.wireOp",EDGE,"E8");var subQ1=sQuery(id+"F0.wireOp",EDGE,"E5");var subQ2=makeQuery(id+"F0.imprint","INTERSECT",VERTEX,{"derivedFrom":[subQ1,subQ0]});Q34=makeQuery(id+"F0.imprint","IMPRINT",FACE,{"disambiguationData":[TD([[makeQuery(id+"F0.imprint","IMPRINT",EDGE,{"disambiguationData":[TD([[subQ2,1.0]])],"derivedFrom":subQ1}),-1.0]])]});}
            var Q35;
            {var subQ0=sQuery(id+"F0.wireOp",EDGE,"E16");var subQ1=sQuery(id+"F0.wireOp",EDGE,"E6");var subQ2=makeQuery(id+"F0.imprint","INTERSECT",VERTEX,{"derivedFrom":[subQ1,subQ0]});Q35=makeQuery(id+"F0.imprint","IMPRINT",FACE,{"disambiguationData":[TD([[makeQuery(id+"F0.imprint","IMPRINT",EDGE,{"disambiguationData":[TD([[subQ2,-1.0]])],"derivedFrom":subQ1}),-1.0]])]});}
            var Q36;
            {var subQ0=sQuery(id+"F0.wireOp",EDGE,"E16");var subQ1=sQuery(id+"F0.wireOp",EDGE,"E7");var subQ2=makeQuery(id+"F0.imprint","INTERSECT",VERTEX,{"derivedFrom":[subQ1,subQ0]});Q36=makeQuery(id+"F0.imprint","IMPRINT",FACE,{"disambiguationData":[TD([[makeQuery(id+"F0.imprint","IMPRINT",EDGE,{"disambiguationData":[TD([[subQ2,-1.0]])],"derivedFrom":subQ1}),-1.0]])]});}
            var Q37;
            {var subQ0=sQuery(id+"F0.wireOp",EDGE,"E16");var subQ1=sQuery(id+"F0.wireOp",EDGE,"E5");var subQ2=makeQuery(id+"F0.imprint","INTERSECT",VERTEX,{"derivedFrom":[subQ1,subQ0]});Q37=makeQuery(id+"F0.imprint","IMPRINT",FACE,{"disambiguationData":[TD([[makeQuery(id+"F0.imprint","IMPRINT",EDGE,{"disambiguationData":[TD([[subQ2,-1.0]])],"derivedFrom":subQ1}),-1.0]])]});}
            var Q38;
            {var subQ0=sQuery(id+"F0.wireOp",EDGE,"E17");var subQ1=sQuery(id+"F0.wireOp",EDGE,"E7");var subQ2=makeQuery(id+"F0.imprint","INTERSECT",VERTEX,{"derivedFrom":[subQ1,subQ0]});Q38=makeQuery(id+"F0.imprint","IMPRINT",FACE,{"disambiguationData":[TD([[makeQuery(id+"F0.imprint","IMPRINT",EDGE,{"disambiguationData":[TD([[subQ2,-1.0]])],"derivedFrom":subQ1}),-1.0]])]});}
            var Q39;
            Q39=makeQuery(id+"F0.imprint","IMPRINT",FACE,{"disambiguationData":[TD([[makeQuery(id+"F0.imprint","IMPRINT",EDGE,{"derivedFrom":sQuery(id+"F0.wireOp",EDGE,"rSFpJtmx-QRcT-HHAU-37F1-OMRx7onwc3MB.bottom")}),-1.0]])]});
            var Q40;
            {var subQ0=sQuery(id+"F0.wireOp",EDGE,"E16");var subQ1=sQuery(id+"F0.wireOp",EDGE,"E4");var subQ2=makeQuery(id+"F0.imprint","INTERSECT",VERTEX,{"derivedFrom":[subQ1,subQ0]});Q40=makeQuery(id+"F0.imprint","IMPRINT",FACE,{"disambiguationData":[TD([[makeQuery(id+"F0.imprint","IMPRINT",EDGE,{"disambiguationData":[TD([[subQ2,-1.0]])],"derivedFrom":subQ1}),-1.0]])]});}
            var Q41;
            {var subQ0=sQuery(id+"F0.wireOp",EDGE,"E16");var subQ1=sQuery(id+"F0.wireOp",EDGE,"E4");var subQ2=makeQuery(id+"F0.imprint","INTERSECT",VERTEX,{"derivedFrom":[subQ1,subQ0]});Q41=makeQuery(id+"F0.imprint","IMPRINT",FACE,{"disambiguationData":[TD([[makeQuery(id+"F0.imprint","IMPRINT",EDGE,{"disambiguationData":[TD([[subQ2,-1.0]])],"derivedFrom":subQ1}),1.0]])]});}
            var Q42;
            {var subQ3=sQuery(id+"F0.wireOp",EDGE,"E4");var subQ7=sQuery(id+"F0.wireOp",EDGE,"E17");var subQ9=makeQuery(id+"F0.imprint","INTERSECT",VERTEX,{"derivedFrom":[subQ3,subQ7]});Q42=makeQuery(id+"F0.imprint","IMPRINT",FACE,{"disambiguationData":[TD([[makeQuery(id+"F0.imprint","IMPRINT",EDGE,{"disambiguationData":[TD([[subQ9,-1.0]])],"derivedFrom":subQ3}),-1.0]])]});}
            var Q43;
            {var subQ1=sQuery(id+"F0.wireOp",EDGE,"E13");var subQ5=sQuery(id+"F0.wireOp",EDGE,"E4");var subQ6=makeQuery(id+"F0.imprint","INTERSECT",VERTEX,{"derivedFrom":[subQ5,subQ1]});Q43=makeQuery(id+"F0.imprint","IMPRINT",FACE,{"disambiguationData":[TD([[makeQuery(id+"F0.imprint","IMPRINT",EDGE,{"disambiguationData":[TD([[subQ6,1.0]])],"derivedFrom":subQ5}),1.0]])]});}
            var Q44;
            {var subQ0=sQuery(id+"F0.wireOp",EDGE,"E17");var subQ1=sQuery(id+"F0.wireOp",EDGE,"E5");var subQ2=makeQuery(id+"F0.imprint","INTERSECT",VERTEX,{"derivedFrom":[subQ1,subQ0]});Q44=makeQuery(id+"F0.imprint","IMPRINT",FACE,{"disambiguationData":[TD([[makeQuery(id+"F0.imprint","IMPRINT",EDGE,{"disambiguationData":[TD([[subQ2,-1.0]])],"derivedFrom":subQ1}),-1.0]])]});}
            var Q45;
            {var subQ0=sQuery(id+"F0.wireOp",EDGE,"E17");var subQ1=sQuery(id+"F0.wireOp",EDGE,"E4");var subQ2=makeQuery(id+"F0.imprint","INTERSECT",VERTEX,{"derivedFrom":[subQ1,subQ0]});Q45=makeQuery(id+"F0.imprint","IMPRINT",FACE,{"disambiguationData":[TD([[makeQuery(id+"F0.imprint","IMPRINT",EDGE,{"disambiguationData":[TD([[subQ2,-1.0]])],"derivedFrom":subQ1}),1.0]])]});}
            var Q46;
            {var subQ0=sQuery(id+"F0.wireOp",EDGE,"E14");var subQ1=sQuery(id+"F0.wireOp",EDGE,"E11");var subQ2=makeQuery(id+"F0.imprint","INTERSECT",VERTEX,{"derivedFrom":[subQ1,subQ0]});Q46=makeQuery(id+"F0.imprint","IMPRINT",FACE,{"disambiguationData":[TD([[makeQuery(id+"F0.imprint","IMPRINT",EDGE,{"disambiguationData":[TD([[subQ2,1.0]])],"derivedFrom":subQ1}),-1.0]])]});}
            var Q47;
            {var subQ0=sQuery(id+"F0.wireOp",EDGE,"E17");var subQ1=sQuery(id+"F0.wireOp",EDGE,"E11");var subQ2=makeQuery(id+"F0.imprint","INTERSECT",VERTEX,{"derivedFrom":[subQ1,subQ0]});Q47=makeQuery(id+"F0.imprint","IMPRINT",FACE,{"disambiguationData":[TD([[makeQuery(id+"F0.imprint","IMPRINT",EDGE,{"disambiguationData":[TD([[subQ2,-1.0]])],"derivedFrom":subQ1}),-1.0]])]});}
            var Q48;
            {var subQ0=sQuery(id+"F0.wireOp",EDGE,"E17");var subQ1=sQuery(id+"F0.wireOp",EDGE,"E13");var subQ2=makeQuery(id+"F0.imprint","INTERSECT",VERTEX,{"derivedFrom":[subQ1,subQ0]});Q48=makeQuery(id+"F0.imprint","IMPRINT",FACE,{"disambiguationData":[TD([[makeQuery(id+"F0.imprint","IMPRINT",EDGE,{"disambiguationData":[TD([[subQ2,-1.0]])],"derivedFrom":subQ1}),-1.0]])]});}
            var Q49;
            Q49=makeQuery(id+"F0.imprint","IMPRINT",FACE,{"disambiguationData":[TD([[makeQuery(id+"F0.imprint","IMPRINT",EDGE,{"derivedFrom":sQuery(id+"F0.wireOp",EDGE,"E18")}),-1.0]])]});
            var Q50;
            Q50=makeQuery(id+"F0.imprint","IMPRINT",FACE,{"disambiguationData":[TD([[makeQuery(id+"F0.imprint","IMPRINT",EDGE,{"derivedFrom":sQuery(id+"F0.wireOp",EDGE,"E18")}),1.0]])]});
            var Q51;
            Q51=sQuery(id+"F1.wireOp",VERTEX,"E21.start");
            extrude(context, id + "F3", {"entities" : qUnion([Q0, Q1, Q2, Q3, Q4, Q5, Q6, Q7, Q8, Q9, Q10, Q11, Q12, Q13, Q14, Q15, Q16, Q17, Q18, Q19, Q20, Q21, Q22, Q23, Q24, Q25, Q26, Q27, Q28, Q29, Q30, Q31, Q32, Q33, Q34, Q35, Q36, Q37, Q38, Q39, Q40, Q41, Q42, Q43, Q44, Q45, Q46, Q47, Q48, Q49, Q50]), "operationType" : NewBodyOperationType.ADD, "endBound" : BoundingType.UP_TO_VERTEX, "oppositeDirection" : true, "depth" : 25 * mm, "endBoundEntityVertex" : qUnion([Q51]), "offsetDistance" : 25 * mm});
        }
        {
            var Q0;
            {var subQ0=sQuery(id+"F0.wireOp",EDGE,"E1");Q0=makeQuery(id+"F2.opExtrude","CAP_EDGE",EDGE,{"disambiguationData":[OSD([subQ0]),TDD([makeQuery(id+"F0.imprint","IMPRINT",EDGE,{"disambiguationData":[TD([[makeQuery(id+"F0.imprint","INTERSECT",VERTEX,{"derivedFrom":[subQ0,sQuery(id+"F0.wireOp",EDGE,"E4")]}),-1.0]])],"derivedFrom":subQ0})])],"isStart":false});}
            var Q1;
            {var subQ0=sQuery(id+"F0.wireOp",EDGE,"E1");Q1=makeQuery(id+"F2.opExtrude","CAP_EDGE",EDGE,{"disambiguationData":[OSD([subQ0]),TDD([makeQuery(id+"F0.imprint","IMPRINT",EDGE,{"disambiguationData":[TD([[makeQuery(id+"F0.imprint","INTERSECT",VERTEX,{"derivedFrom":[subQ0,sQuery(id+"F0.wireOp",EDGE,"E9")]}),1.0]])],"derivedFrom":subQ0})])],"isStart":false});}
            var Q2;
            {var subQ0=sQuery(id+"F0.wireOp",EDGE,"E1");Q2=makeQuery(id+"F2.opExtrude","CAP_EDGE",EDGE,{"disambiguationData":[OSD([subQ0]),TDD([makeQuery(id+"F0.imprint","IMPRINT",EDGE,{"disambiguationData":[TD([[makeQuery(id+"F0.imprint","INTERSECT",VERTEX,{"derivedFrom":[subQ0,sQuery(id+"F0.wireOp",EDGE,"E10")]}),-1.0]])],"derivedFrom":subQ0})])],"isStart":false});}
            var Q3;
            {var subQ0=sQuery(id+"F0.wireOp",EDGE,"E1");Q3=makeQuery(id+"F2.opExtrude","CAP_EDGE",EDGE,{"disambiguationData":[OSD([subQ0]),TDD([makeQuery(id+"F0.imprint","IMPRINT",EDGE,{"disambiguationData":[TD([[makeQuery(id+"F0.imprint","INTERSECT",VERTEX,{"derivedFrom":[subQ0,sQuery(id+"F0.wireOp",EDGE,"E12")]}),-1.0]])],"derivedFrom":subQ0})])],"isStart":false});}
            var Q4;
            {var subQ0=sQuery(id+"F0.wireOp",EDGE,"E1");Q4=makeQuery(id+"F2.opExtrude","CAP_EDGE",EDGE,{"disambiguationData":[OSD([subQ0]),TDD([makeQuery(id+"F0.imprint","IMPRINT",EDGE,{"disambiguationData":[TD([[makeQuery(id+"F0.imprint","INTERSECT",VERTEX,{"derivedFrom":[subQ0,sQuery(id+"F0.wireOp",EDGE,"E14")]}),-1.0]])],"derivedFrom":subQ0})])],"isStart":false});}
            var Q5;
            {var subQ0=sQuery(id+"F0.wireOp",EDGE,"E1");Q5=makeQuery(id+"F2.opExtrude","CAP_EDGE",EDGE,{"disambiguationData":[OSD([subQ0]),TDD([makeQuery(id+"F0.imprint","IMPRINT",EDGE,{"disambiguationData":[TD([[makeQuery(id+"F0.imprint","INTERSECT",VERTEX,{"derivedFrom":[subQ0,sQuery(id+"F0.wireOp",EDGE,"E6")]}),-1.0]])],"derivedFrom":subQ0})])],"isStart":false});}
            chamfer(context, id + "F4", {"entities" : qUnion([Q0, Q1, Q2, Q3, Q4, Q5]), "chamferType" : ChamferType.TWO_OFFSETS, "width1" : 4 * mm, "oppositeDirection" : false, "width2" : 2 * mm, "tangentPropagation" : true});
        }
        {
            var Q0;
            Q0=makeQuery(id+"F3.opExtrude","SWEPT_FACE",FACE,{"disambiguationData":[OSD([sQuery(id+"F0.wireOp",EDGE,"E0")])]});
            var Q1;
            Q1=makeQuery(id+"F2.opExtrude","CAP_EDGE",EDGE,{"disambiguationData":[OSD([sQuery(id+"F0.wireOp",EDGE,"E17")])],"isStart":false});
            var Q2;
            {var subQ0=sQuery(id+"F0.wireOp",EDGE,"E1");var subQ1=makeQuery(id+"F0.imprint","IMPRINT",EDGE,{"disambiguationData":[TD([[makeQuery(id+"F0.imprint","INTERSECT",VERTEX,{"derivedFrom":[subQ0,sQuery(id+"F0.wireOp",EDGE,"E6")]}),-1.0]])],"derivedFrom":subQ0});Q2=makeQuery(id+"F4.opChamfer","BLEND_EDGE",EDGE,{"blendedFrom":[makeQuery(id+"F2.opExtrude","CAP_EDGE",EDGE,{"disambiguationData":[OSD([subQ0]),TDD([subQ1])],"isStart":false}),makeQuery(id+"F2.opExtrude","SWEPT_FACE",FACE,{"disambiguationData":[OSD([subQ0]),TDD([subQ1])]})],"blendedInto":[makeQuery(id+"F2.opExtrude","SWEPT_FACE",FACE,{"disambiguationData":[OSD([subQ0]),TDD([subQ1])]})]});}
            var Q3;
            Q3=makeQuery(id+"F2.opExtrude","SWEPT_EDGE",EDGE,{"disambiguationData":[OSD([sQuery(id+"F0.wireOp",EDGE,"E1"),sQuery(id+"F0.wireOp",EDGE,"E5")])]});
            var Q4;
            Q4=makeQuery(id+"F2.opExtrude","SWEPT_EDGE",EDGE,{"disambiguationData":[OSD([sQuery(id+"F0.wireOp",EDGE,"E1"),sQuery(id+"F0.wireOp",EDGE,"E4")])]});
            var Q5;
            {var subQ0=sQuery(id+"F0.wireOp",EDGE,"E1");var subQ1=makeQuery(id+"F0.imprint","IMPRINT",EDGE,{"disambiguationData":[TD([[makeQuery(id+"F0.imprint","INTERSECT",VERTEX,{"derivedFrom":[subQ0,sQuery(id+"F0.wireOp",EDGE,"E4")]}),-1.0]])],"derivedFrom":subQ0});Q5=makeQuery(id+"F4.opChamfer","BLEND_EDGE",EDGE,{"blendedFrom":[makeQuery(id+"F2.opExtrude","CAP_EDGE",EDGE,{"disambiguationData":[OSD([subQ0]),TDD([subQ1])],"isStart":false}),makeQuery(id+"F2.opExtrude","SWEPT_FACE",FACE,{"disambiguationData":[OSD([subQ0]),TDD([subQ1])]})],"blendedInto":[makeQuery(id+"F2.opExtrude","SWEPT_FACE",FACE,{"disambiguationData":[OSD([subQ0]),TDD([subQ1])]})]});}
            var Q6;
            {var subQ0=sQuery(id+"F0.wireOp",EDGE,"E4");var subQ1=sQuery(id+"F0.wireOp",EDGE,"E1");Q6=makeQuery(id+"F4.opChamfer","BLEND_EDGE",EDGE,{"blendedFrom":[makeQuery(id+"F2.opExtrude","CAP_EDGE",EDGE,{"disambiguationData":[OSD([subQ1]),TDD([makeQuery(id+"F0.imprint","IMPRINT",EDGE,{"disambiguationData":[TD([[makeQuery(id+"F0.imprint","INTERSECT",VERTEX,{"derivedFrom":[subQ1,subQ0]}),-1.0]])],"derivedFrom":subQ1})])],"isStart":false}),makeQuery(id+"F2.opExtrude","SWEPT_FACE",FACE,{"disambiguationData":[OSD([subQ0])]})],"blendedInto":[makeQuery(id+"F2.opExtrude","SWEPT_FACE",FACE,{"disambiguationData":[OSD([subQ0])]})]});}
            var Q7;
            {var subQ0=sQuery(id+"F0.wireOp",EDGE,"E5");var subQ1=sQuery(id+"F0.wireOp",EDGE,"E1");Q7=makeQuery(id+"F4.opChamfer","BLEND_EDGE",EDGE,{"blendedFrom":[makeQuery(id+"F2.opExtrude","CAP_EDGE",EDGE,{"disambiguationData":[OSD([subQ1]),TDD([makeQuery(id+"F0.imprint","IMPRINT",EDGE,{"disambiguationData":[TD([[makeQuery(id+"F0.imprint","INTERSECT",VERTEX,{"derivedFrom":[subQ1,sQuery(id+"F0.wireOp",EDGE,"E4")]}),-1.0]])],"derivedFrom":subQ1})])],"isStart":false}),makeQuery(id+"F2.opExtrude","SWEPT_FACE",FACE,{"disambiguationData":[OSD([subQ0])]})],"blendedInto":[makeQuery(id+"F2.opExtrude","SWEPT_FACE",FACE,{"disambiguationData":[OSD([subQ0])]})]});}
            var Q8;
            {var subQ0=sQuery(id+"F0.wireOp",EDGE,"E6");var subQ1=sQuery(id+"F0.wireOp",EDGE,"E1");Q8=makeQuery(id+"F4.opChamfer","BLEND_EDGE",EDGE,{"blendedFrom":[makeQuery(id+"F2.opExtrude","CAP_EDGE",EDGE,{"disambiguationData":[OSD([subQ1]),TDD([makeQuery(id+"F0.imprint","IMPRINT",EDGE,{"disambiguationData":[TD([[makeQuery(id+"F0.imprint","INTERSECT",VERTEX,{"derivedFrom":[subQ1,subQ0]}),-1.0]])],"derivedFrom":subQ1})])],"isStart":false}),makeQuery(id+"F2.opExtrude","SWEPT_FACE",FACE,{"disambiguationData":[OSD([subQ0])]})],"blendedInto":[makeQuery(id+"F2.opExtrude","SWEPT_FACE",FACE,{"disambiguationData":[OSD([subQ0])]})]});}
            var Q9;
            {var subQ0=sQuery(id+"F0.wireOp",EDGE,"E7");var subQ1=sQuery(id+"F0.wireOp",EDGE,"E1");Q9=makeQuery(id+"F4.opChamfer","BLEND_EDGE",EDGE,{"blendedFrom":[makeQuery(id+"F2.opExtrude","CAP_EDGE",EDGE,{"disambiguationData":[OSD([subQ1]),TDD([makeQuery(id+"F0.imprint","IMPRINT",EDGE,{"disambiguationData":[TD([[makeQuery(id+"F0.imprint","INTERSECT",VERTEX,{"derivedFrom":[subQ1,sQuery(id+"F0.wireOp",EDGE,"E6")]}),-1.0]])],"derivedFrom":subQ1})])],"isStart":false}),makeQuery(id+"F2.opExtrude","SWEPT_FACE",FACE,{"disambiguationData":[OSD([subQ0])]})],"blendedInto":[makeQuery(id+"F2.opExtrude","SWEPT_FACE",FACE,{"disambiguationData":[OSD([subQ0])]})]});}
            var Q10;
            {var subQ0=sQuery(id+"F0.wireOp",EDGE,"E14");var subQ1=sQuery(id+"F0.wireOp",EDGE,"E1");Q10=makeQuery(id+"F4.opChamfer","BLEND_EDGE",EDGE,{"blendedFrom":[makeQuery(id+"F2.opExtrude","CAP_EDGE",EDGE,{"disambiguationData":[OSD([subQ1]),TDD([makeQuery(id+"F0.imprint","IMPRINT",EDGE,{"disambiguationData":[TD([[makeQuery(id+"F0.imprint","INTERSECT",VERTEX,{"derivedFrom":[subQ1,subQ0]}),-1.0]])],"derivedFrom":subQ1})])],"isStart":false}),makeQuery(id+"F2.opExtrude","SWEPT_FACE",FACE,{"disambiguationData":[OSD([subQ0])]})],"blendedInto":[makeQuery(id+"F2.opExtrude","SWEPT_FACE",FACE,{"disambiguationData":[OSD([subQ0])]})]});}
            var Q11;
            {var subQ0=sQuery(id+"F0.wireOp",EDGE,"E1");var subQ1=makeQuery(id+"F0.imprint","IMPRINT",EDGE,{"disambiguationData":[TD([[makeQuery(id+"F0.imprint","INTERSECT",VERTEX,{"derivedFrom":[subQ0,sQuery(id+"F0.wireOp",EDGE,"E14")]}),-1.0]])],"derivedFrom":subQ0});Q11=makeQuery(id+"F4.opChamfer","BLEND_EDGE",EDGE,{"blendedFrom":[makeQuery(id+"F2.opExtrude","CAP_EDGE",EDGE,{"disambiguationData":[OSD([subQ0]),TDD([subQ1])],"isStart":false}),makeQuery(id+"F2.opExtrude","SWEPT_FACE",FACE,{"disambiguationData":[OSD([subQ0]),TDD([subQ1])]})],"blendedInto":[makeQuery(id+"F2.opExtrude","SWEPT_FACE",FACE,{"disambiguationData":[OSD([subQ0]),TDD([subQ1])]})]});}
            var Q12;
            {var subQ0=sQuery(id+"F0.wireOp",EDGE,"E15");var subQ1=sQuery(id+"F0.wireOp",EDGE,"E1");Q12=makeQuery(id+"F4.opChamfer","BLEND_EDGE",EDGE,{"blendedFrom":[makeQuery(id+"F2.opExtrude","CAP_EDGE",EDGE,{"disambiguationData":[OSD([subQ1]),TDD([makeQuery(id+"F0.imprint","IMPRINT",EDGE,{"disambiguationData":[TD([[makeQuery(id+"F0.imprint","INTERSECT",VERTEX,{"derivedFrom":[subQ1,sQuery(id+"F0.wireOp",EDGE,"E14")]}),-1.0]])],"derivedFrom":subQ1})])],"isStart":false}),makeQuery(id+"F2.opExtrude","SWEPT_FACE",FACE,{"disambiguationData":[OSD([subQ0])]})],"blendedInto":[makeQuery(id+"F2.opExtrude","SWEPT_FACE",FACE,{"disambiguationData":[OSD([subQ0])]})]});}
            var Q13;
            Q13=makeQuery(id+"F2.opExtrude","SWEPT_EDGE",EDGE,{"disambiguationData":[OSD([sQuery(id+"F0.wireOp",EDGE,"E1"),sQuery(id+"F0.wireOp",EDGE,"E15")])]});
            var Q14;
            Q14=makeQuery(id+"F2.opExtrude","SWEPT_EDGE",EDGE,{"disambiguationData":[OSD([sQuery(id+"F0.wireOp",EDGE,"E1"),sQuery(id+"F0.wireOp",EDGE,"E14")])]});
            var Q15;
            {var subQ0=sQuery(id+"F0.wireOp",EDGE,"E1");Q15=makeQuery(id+"F2.opExtrude","SWEPT_FACE",FACE,{"disambiguationData":[OSD([subQ0]),TDD([makeQuery(id+"F0.imprint","IMPRINT",EDGE,{"disambiguationData":[TD([[makeQuery(id+"F0.imprint","INTERSECT",VERTEX,{"derivedFrom":[subQ0,sQuery(id+"F0.wireOp",EDGE,"E12")]}),-1.0]])],"derivedFrom":subQ0})])]});}
            var Q16;
            {var subQ0=sQuery(id+"F0.wireOp",EDGE,"E12");var subQ1=sQuery(id+"F0.wireOp",EDGE,"E1");Q16=makeQuery(id+"F4.opChamfer","BLEND_EDGE",EDGE,{"blendedFrom":[makeQuery(id+"F2.opExtrude","CAP_EDGE",EDGE,{"disambiguationData":[OSD([subQ1]),TDD([makeQuery(id+"F0.imprint","IMPRINT",EDGE,{"disambiguationData":[TD([[makeQuery(id+"F0.imprint","INTERSECT",VERTEX,{"derivedFrom":[subQ1,subQ0]}),-1.0]])],"derivedFrom":subQ1})])],"isStart":false}),makeQuery(id+"F2.opExtrude","SWEPT_FACE",FACE,{"disambiguationData":[OSD([subQ0])]})],"blendedInto":[makeQuery(id+"F2.opExtrude","SWEPT_FACE",FACE,{"disambiguationData":[OSD([subQ0])]})]});}
            var Q17;
            {var subQ0=sQuery(id+"F0.wireOp",EDGE,"E13");var subQ1=sQuery(id+"F0.wireOp",EDGE,"E1");Q17=makeQuery(id+"F4.opChamfer","BLEND_EDGE",EDGE,{"blendedFrom":[makeQuery(id+"F2.opExtrude","CAP_EDGE",EDGE,{"disambiguationData":[OSD([subQ1]),TDD([makeQuery(id+"F0.imprint","IMPRINT",EDGE,{"disambiguationData":[TD([[makeQuery(id+"F0.imprint","INTERSECT",VERTEX,{"derivedFrom":[subQ1,sQuery(id+"F0.wireOp",EDGE,"E12")]}),-1.0]])],"derivedFrom":subQ1})])],"isStart":false}),makeQuery(id+"F2.opExtrude","SWEPT_FACE",FACE,{"disambiguationData":[OSD([subQ0])]})],"blendedInto":[makeQuery(id+"F2.opExtrude","SWEPT_FACE",FACE,{"disambiguationData":[OSD([subQ0])]})]});}
            var Q18;
            {var subQ0=sQuery(id+"F0.wireOp",EDGE,"E1");Q18=makeQuery(id+"F2.opExtrude","SWEPT_FACE",FACE,{"disambiguationData":[OSD([subQ0]),TDD([makeQuery(id+"F0.imprint","IMPRINT",EDGE,{"disambiguationData":[TD([[makeQuery(id+"F0.imprint","INTERSECT",VERTEX,{"derivedFrom":[subQ0,sQuery(id+"F0.wireOp",EDGE,"E10")]}),-1.0]])],"derivedFrom":subQ0})])]});}
            var Q19;
            {var subQ0=sQuery(id+"F0.wireOp",EDGE,"E11");var subQ1=sQuery(id+"F0.wireOp",EDGE,"E1");Q19=makeQuery(id+"F4.opChamfer","BLEND_EDGE",EDGE,{"blendedFrom":[makeQuery(id+"F2.opExtrude","CAP_EDGE",EDGE,{"disambiguationData":[OSD([subQ1]),TDD([makeQuery(id+"F0.imprint","IMPRINT",EDGE,{"disambiguationData":[TD([[makeQuery(id+"F0.imprint","INTERSECT",VERTEX,{"derivedFrom":[subQ1,sQuery(id+"F0.wireOp",EDGE,"E10")]}),-1.0]])],"derivedFrom":subQ1})])],"isStart":false}),makeQuery(id+"F2.opExtrude","SWEPT_FACE",FACE,{"disambiguationData":[OSD([subQ0])]})],"blendedInto":[makeQuery(id+"F2.opExtrude","SWEPT_FACE",FACE,{"disambiguationData":[OSD([subQ0])]})]});}
            var Q20;
            {var subQ0=sQuery(id+"F0.wireOp",EDGE,"E10");var subQ1=sQuery(id+"F0.wireOp",EDGE,"E1");Q20=makeQuery(id+"F4.opChamfer","BLEND_EDGE",EDGE,{"blendedFrom":[makeQuery(id+"F2.opExtrude","CAP_EDGE",EDGE,{"disambiguationData":[OSD([subQ1]),TDD([makeQuery(id+"F0.imprint","IMPRINT",EDGE,{"disambiguationData":[TD([[makeQuery(id+"F0.imprint","INTERSECT",VERTEX,{"derivedFrom":[subQ1,subQ0]}),-1.0]])],"derivedFrom":subQ1})])],"isStart":false}),makeQuery(id+"F2.opExtrude","SWEPT_FACE",FACE,{"disambiguationData":[OSD([subQ0])]})],"blendedInto":[makeQuery(id+"F2.opExtrude","SWEPT_FACE",FACE,{"disambiguationData":[OSD([subQ0])]})]});}
            var Q21;
            {var subQ0=sQuery(id+"F0.wireOp",EDGE,"E1");Q21=makeQuery(id+"F2.opExtrude","SWEPT_FACE",FACE,{"disambiguationData":[OSD([subQ0]),TDD([makeQuery(id+"F0.imprint","IMPRINT",EDGE,{"disambiguationData":[TD([[makeQuery(id+"F0.imprint","INTERSECT",VERTEX,{"derivedFrom":[subQ0,sQuery(id+"F0.wireOp",EDGE,"E9")]}),1.0]])],"derivedFrom":subQ0})])]});}
            var Q22;
            {var subQ0=sQuery(id+"F0.wireOp",EDGE,"E9");var subQ1=sQuery(id+"F0.wireOp",EDGE,"E1");Q22=makeQuery(id+"F4.opChamfer","BLEND_EDGE",EDGE,{"blendedFrom":[makeQuery(id+"F2.opExtrude","CAP_EDGE",EDGE,{"disambiguationData":[OSD([subQ1]),TDD([makeQuery(id+"F0.imprint","IMPRINT",EDGE,{"disambiguationData":[TD([[makeQuery(id+"F0.imprint","INTERSECT",VERTEX,{"derivedFrom":[subQ1,subQ0]}),1.0]])],"derivedFrom":subQ1})])],"isStart":false}),makeQuery(id+"F2.opExtrude","SWEPT_FACE",FACE,{"disambiguationData":[OSD([subQ0])]})],"blendedInto":[makeQuery(id+"F2.opExtrude","SWEPT_FACE",FACE,{"disambiguationData":[OSD([subQ0])]})]});}
            var Q23;
            {var subQ0=sQuery(id+"F0.wireOp",EDGE,"E8");var subQ1=sQuery(id+"F0.wireOp",EDGE,"E1");Q23=makeQuery(id+"F4.opChamfer","BLEND_EDGE",EDGE,{"blendedFrom":[makeQuery(id+"F2.opExtrude","CAP_EDGE",EDGE,{"disambiguationData":[OSD([subQ1]),TDD([makeQuery(id+"F0.imprint","IMPRINT",EDGE,{"disambiguationData":[TD([[makeQuery(id+"F0.imprint","INTERSECT",VERTEX,{"derivedFrom":[subQ1,sQuery(id+"F0.wireOp",EDGE,"E9")]}),1.0]])],"derivedFrom":subQ1})])],"isStart":false}),makeQuery(id+"F2.opExtrude","SWEPT_FACE",FACE,{"disambiguationData":[OSD([subQ0])]})],"blendedInto":[makeQuery(id+"F2.opExtrude","SWEPT_FACE",FACE,{"disambiguationData":[OSD([subQ0])]})]});}
            var Q24;
            {var subQ0=sQuery(id+"F0.wireOp",EDGE,"E16");Q24=makeQuery(id+"F2.opExtrude","SWEPT_FACE",FACE,{"disambiguationData":[OSD([subQ0]),TDD([makeQuery(id+"F0.imprint","IMPRINT",EDGE,{"disambiguationData":[TD([[makeQuery(id+"F0.imprint","INTERSECT",VERTEX,{"derivedFrom":[sQuery(id+"F0.wireOp",EDGE,"E4"),subQ0]}),1.0]])],"derivedFrom":subQ0})])]});}
            var Q25;
            {var subQ0=sQuery(id+"F0.wireOp",EDGE,"E16");Q25=makeQuery(id+"F2.opExtrude","SWEPT_FACE",FACE,{"disambiguationData":[OSD([subQ0]),TDD([makeQuery(id+"F0.imprint","IMPRINT",EDGE,{"disambiguationData":[TD([[makeQuery(id+"F0.imprint","INTERSECT",VERTEX,{"derivedFrom":[sQuery(id+"F0.wireOp",EDGE,"E5"),subQ0]}),-1.0]])],"derivedFrom":subQ0})])]});}
            var Q26;
            {var subQ0=sQuery(id+"F0.wireOp",EDGE,"E16");Q26=makeQuery(id+"F2.opExtrude","SWEPT_FACE",FACE,{"disambiguationData":[OSD([subQ0]),TDD([makeQuery(id+"F0.imprint","IMPRINT",EDGE,{"disambiguationData":[TD([[makeQuery(id+"F0.imprint","INTERSECT",VERTEX,{"derivedFrom":[sQuery(id+"F0.wireOp",EDGE,"E7"),subQ0]}),-1.0]])],"derivedFrom":subQ0})])]});}
            var Q27;
            {var subQ0=sQuery(id+"F0.wireOp",EDGE,"E16");Q27=makeQuery(id+"F2.opExtrude","SWEPT_FACE",FACE,{"disambiguationData":[OSD([subQ0]),TDD([makeQuery(id+"F0.imprint","IMPRINT",EDGE,{"disambiguationData":[TD([[makeQuery(id+"F0.imprint","INTERSECT",VERTEX,{"derivedFrom":[sQuery(id+"F0.wireOp",EDGE,"E9"),subQ0]}),-1.0]])],"derivedFrom":subQ0})])]});}
            var Q28;
            {var subQ0=sQuery(id+"F0.wireOp",EDGE,"E16");Q28=makeQuery(id+"F2.opExtrude","SWEPT_FACE",FACE,{"disambiguationData":[OSD([subQ0]),TDD([makeQuery(id+"F0.imprint","IMPRINT",EDGE,{"disambiguationData":[TD([[makeQuery(id+"F0.imprint","INTERSECT",VERTEX,{"derivedFrom":[sQuery(id+"F0.wireOp",EDGE,"E11"),subQ0]}),-1.0]])],"derivedFrom":subQ0})])]});}
            var Q29;
            {var subQ0=sQuery(id+"F0.wireOp",EDGE,"E16");Q29=makeQuery(id+"F2.opExtrude","SWEPT_FACE",FACE,{"disambiguationData":[OSD([subQ0]),TDD([makeQuery(id+"F0.imprint","IMPRINT",EDGE,{"disambiguationData":[TD([[makeQuery(id+"F0.imprint","INTERSECT",VERTEX,{"derivedFrom":[sQuery(id+"F0.wireOp",EDGE,"E13"),subQ0]}),-1.0]])],"derivedFrom":subQ0})])]});}
            var Q30;
            Q30=makeQuery(id+"F3.opExtrude","CAP_EDGE",EDGE,{"disambiguationData":[OSD([sQuery(id+"F0.wireOp",EDGE,"rSFpJtmx-QRcT-HHAU-37F1-OMRx7onwc3MB.left")])],"isStart":true});
            var Q31;
            Q31=makeQuery(id+"F3.opExtrude","CAP_EDGE",EDGE,{"disambiguationData":[OSD([sQuery(id+"F0.wireOp",EDGE,"rSFpJtmx-QRcT-HHAU-37F1-OMRx7onwc3MB.right")])],"isStart":true});
            var Q32;
            Q32=makeQuery(id+"F3.opExtrude","CAP_EDGE",EDGE,{"disambiguationData":[OSD([sQuery(id+"F0.wireOp",EDGE,"rSFpJtmx-QRcT-HHAU-37F1-OMRx7onwc3MB.top")])],"isStart":true});
            var Q33;
            Q33=makeQuery(id+"F3.opExtrude","CAP_EDGE",EDGE,{"disambiguationData":[OSD([sQuery(id+"F0.wireOp",EDGE,"rSFpJtmx-QRcT-HHAU-37F1-OMRx7onwc3MB.bottom")])],"isStart":true});
            fillet(context, id + "F5", {"entities" : qUnion([Q0, Q1, Q2, Q3, Q4, Q5, Q6, Q7, Q8, Q9, Q10, Q11, Q12, Q13, Q14, Q15, Q16, Q17, Q18, Q19, Q20, Q21, Q22, Q23, Q24, Q25, Q26, Q27, Q28, Q29, Q30, Q31, Q32, Q33]), "radius" : 0.3 * mm, "tangentPropagation" : true, "defaultsChanged" : true, "vertexSettings" : [], "allowEdgeOverflow" : false});
        }
        {
            var Q0;
            Q0=makeQuery(id+"F0.imprint","IMPRINT",FACE,{"disambiguationData":[TD([[makeQuery(id+"F0.imprint","IMPRINT",EDGE,{"derivedFrom":sQuery(id+"F0.wireOp",EDGE,"E18")}),1.0]])]});
            extrude(context, id + "F6", {"entities" : qUnion([Q0]), "operationType" : NewBodyOperationType.ADD, "depth" : 7 * mm, "offsetDistance" : 25 * mm});
        }
    });
